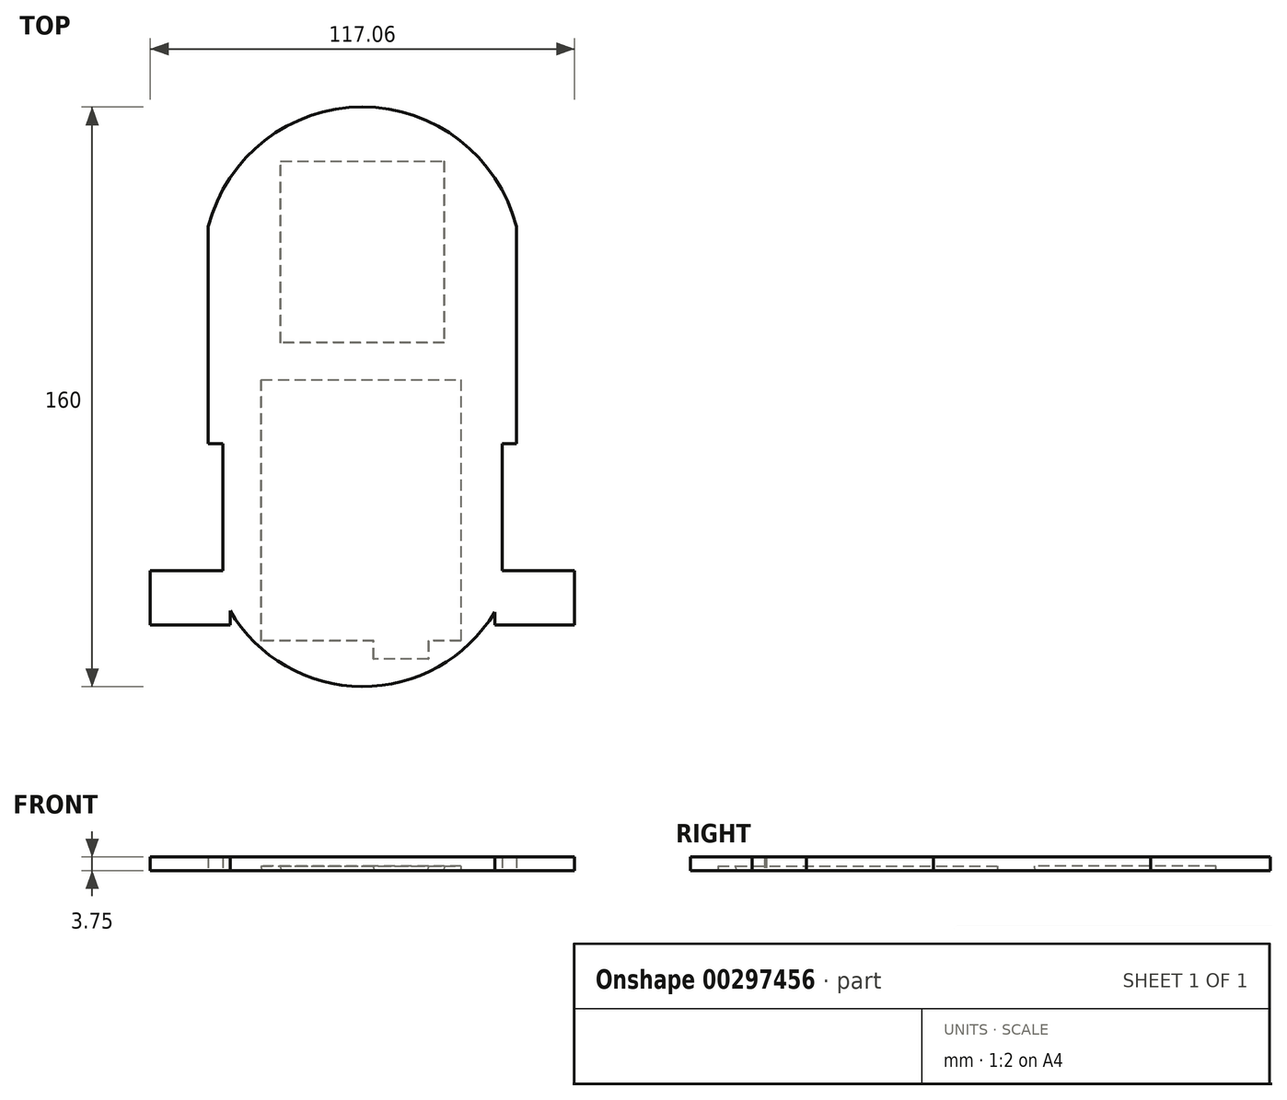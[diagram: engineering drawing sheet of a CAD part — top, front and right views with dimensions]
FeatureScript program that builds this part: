
annotation { "Feature Type Name" : "Feature", "Feature Type Description" : "" }
export const myFeature = defineFeature(function(context is Context, id is Id, definition is map)
    precondition{}
    {
        {
            var Q0;
            Q0=qCreatedBy(makeId("Top.planeOp"),FACE);
            var sketch = newSketch(context, id + "F0", { "sketchPlane" : qUnion([Q0])});
            skLineSegment(sketch, "E0.left", {"start": v(42.5, 30) * mm, "end": v(42.5, -30) * mm});
            skLineSegment(sketch, "E0.right", {"start": v(-42.5, 30) * mm, "end": v(-42.5, -30) * mm});
            skPoint(sketch, "E0.middle", {"position": v(0, 0) * mm});
            skArc(sketch, "E1", {"start": v(42.5, 30) * mm, "mid": v(0, 62.96) * mm, "end": v(-42.5, 30) * mm});
            skLineSegment(sketch, "E2.bottom", {"start": v(66.5, -30) * mm, "end": v(42.5, -30) * mm});
            skLineSegment(sketch, "E2.top", {"start": v(66.5, -80) * mm, "end": v(36.5, -80) * mm});
            skLineSegment(sketch, "E2.left", {"start": v(66.5, -30) * mm, "end": v(66.5, -80) * mm});
            skLineSegment(sketch, "E3.bottom", {"start": v(-66.5, -30) * mm, "end": v(-42.5, -30) * mm});
            skLineSegment(sketch, "E3.top", {"start": v(-66.5, -80) * mm, "end": v(-36.5, -80) * mm});
            skLineSegment(sketch, "E3.left", {"start": v(-66.5, -30) * mm, "end": v(-66.5, -80) * mm});
            skPoint(sketch, "E4.endSnap0", {"position": v(0, -30) * mm});
            skPoint(sketch, "E5.second.point", {"position": v(0, -12.04) * mm});
            skPoint(sketch, "E5.third.point", {"position": v(-39.19, -70.68) * mm});
            skArc(sketch, "E6.trimOffspring", {"start": v(-36.5, -76.09) * mm, "mid": v(-0.12, -97.04) * mm, "end": v(36.5, -76.52) * mm});
            skLineSegment(sketch, "E7.trimOffspring", {"start": v(-36.5, -76.09) * mm, "end": v(-36.5, -80) * mm});
            skLineSegment(sketch, "E8.trimOffspring", {"start": v(36.5, -76.52) * mm, "end": v(36.5, -80) * mm});
            skSolve(sketch);
        }
        {
            var Q0;
            Q0=makeQuery(id+"F0.imprint","IMPRINT",FACE,{"disambiguationData":[TD([[makeQuery(id+"F0.imprint","IMPRINT",EDGE,{"derivedFrom":sQuery(id+"F0.wireOp",EDGE,"E0.left")}),-1.0]])]});
            extrude(context, id + "F1", {"entities" : qUnion([Q0]), "depth" : 5 * mm});
        }
        {
            var Q0;
            Q0=qCreatedBy(makeId("Top.planeOp"),FACE);
            var sketch = newSketch(context, id + "F2", { "sketchPlane" : qUnion([Q0])});
            skLineSegment(sketch, "E9.top", {"start": v(-27.84, -12.36) * mm, "end": v(27.16, -12.36) * mm});
            skLineSegment(sketch, "E9.left", {"start": v(-27.84, -84.36) * mm, "end": v(-27.84, -12.36) * mm});
            skLineSegment(sketch, "E9.right", {"start": v(27.16, -84.36) * mm, "end": v(27.16, -12.36) * mm});
            skLineSegment(sketch, "E10.top", {"start": v(3.16, -89.36) * mm, "end": v(18.16, -89.36) * mm});
            skLineSegment(sketch, "E10.left", {"start": v(3.16, -84.36) * mm, "end": v(3.16, -89.36) * mm});
            skLineSegment(sketch, "E10.right", {"start": v(18.16, -84.36) * mm, "end": v(18.16, -89.36) * mm});
            skLineSegment(sketch, "E11", {"start": v(-27.84, -12.36) * mm, "end": v(-27.84, -7.36) * mm});
            skLineSegment(sketch, "E12.bottom", {"start": v(22.5, 47.94) * mm, "end": v(-22.5, 47.94) * mm});
            skLineSegment(sketch, "E12.top", {"start": v(22.5, -2.06) * mm, "end": v(-22.5, -2.06) * mm});
            skLineSegment(sketch, "E12.left", {"start": v(22.5, 47.94) * mm, "end": v(22.5, -2.06) * mm});
            skLineSegment(sketch, "E12.right", {"start": v(-22.5, 47.94) * mm, "end": v(-22.5, -2.06) * mm});
            skPoint(sketch, "E12.middle", {"position": v(0, 22.94) * mm});
            skPoint(sketch, "E13.bottom.start.orphan", {"position": v(27.16, -7.36) * mm});
            skLineSegment(sketch, "E14", {"start": v(-27.84, -84.36) * mm, "end": v(3.16, -84.36) * mm});
            skLineSegment(sketch, "E15", {"start": v(18.16, -84.36) * mm, "end": v(27.16, -84.36) * mm});
            skSolve(sketch);
        }
        {
            var Q0;
            Q0=makeQuery(id+"F1.opExtrude","CAP_FACE",FACE,{"disambiguationData":[OSD([sQuery(id+"F0.wireOp",EDGE,"E0.left"),sQuery(id+"F0.wireOp",EDGE,"E0.right"),sQuery(id+"F0.wireOp",EDGE,"E1"),sQuery(id+"F0.wireOp",EDGE,"E2.top"),sQuery(id+"F0.wireOp",EDGE,"E2.left"),sQuery(id+"F0.wireOp",EDGE,"E2.bottom"),sQuery(id+"F0.wireOp",EDGE,"E3.top"),sQuery(id+"F0.wireOp",EDGE,"E3.left"),sQuery(id+"F0.wireOp",EDGE,"E3.bottom"),sQuery(id+"F0.wireOp",EDGE,"E6.trimOffspring"),sQuery(id+"F0.wireOp",EDGE,"E7.trimOffspring"),sQuery(id+"F0.wireOp",EDGE,"E8.trimOffspring")])],"isStart":false});
            var Q1;
            Q1 = qSketchRegion(id + "F2", true);
            extrude(context, id + "F3", {"entities" : qUnion([Q0, Q1]), "operationType" : NewBodyOperationType.REMOVE, "endBound" : BoundingType.SYMMETRIC, "depth" : 2.5 * mm, "hasDraft" : true, "draftAngle" : 3 * degree});
        }
        {
            var Q0;
            Q0=qCreatedBy(makeId("Top.planeOp"),FACE);
            var sketch = newSketch(context, id + "F4", { "sketchPlane" : qUnion([Q0])});
            skLineSegment(sketch, "E16.bottom", {"start": v(58.53, -65) * mm, "end": v(38.53, -64.97) * mm});
            skLineSegment(sketch, "E16.right", {"start": v(38.53, -64.97) * mm, "end": v(38.53, -30) * mm});
            skLineSegment(sketch, "E17.top", {"start": v(58.53, -80) * mm, "end": v(66.5, -80) * mm});
            skLineSegment(sketch, "E17.left", {"start": v(58.53, -65) * mm, "end": v(58.53, -80) * mm});
            skLineSegment(sketch, "E18.top", {"start": v(38.53, -65) * mm, "end": v(58.53, -65) * mm});
            skLineSegment(sketch, "E18.left", {"start": v(38.53, -30) * mm, "end": v(38.53, -65) * mm});
            skLineSegment(sketch, "E19", {"start": v(38.53, -30) * mm, "end": v(66.5, -30) * mm});
            skLineSegment(sketch, "E20", {"start": v(66.5, -80) * mm, "end": v(66.5, -30) * mm});
            skLineSegment(sketch, "E21.bottom", {"start": v(-66.5, -30) * mm, "end": v(-38.53, -30) * mm});
            skLineSegment(sketch, "E21.top", {"start": v(-58.53, -65) * mm, "end": v(-38.53, -65) * mm});
            skLineSegment(sketch, "E21.right", {"start": v(-38.53, -30) * mm, "end": v(-38.53, -65) * mm});
            skLineSegment(sketch, "E22.top", {"start": v(-66.5, -80) * mm, "end": v(-58.53, -80) * mm});
            skLineSegment(sketch, "E22.right", {"start": v(-58.53, -65) * mm, "end": v(-58.53, -80) * mm});
            skLineSegment(sketch, "E23", {"start": v(-66.5, -30) * mm, "end": v(-66.5, -80) * mm});
            skSolve(sketch);
        }
        {
            var Q0;
            Q0 = qSketchRegion(id + "F4", true);
            extrude(context, id + "F5", {"entities" : qUnion([Q0]), "operationType" : NewBodyOperationType.REMOVE, "depth" : 25 * mm});
        }
    });
